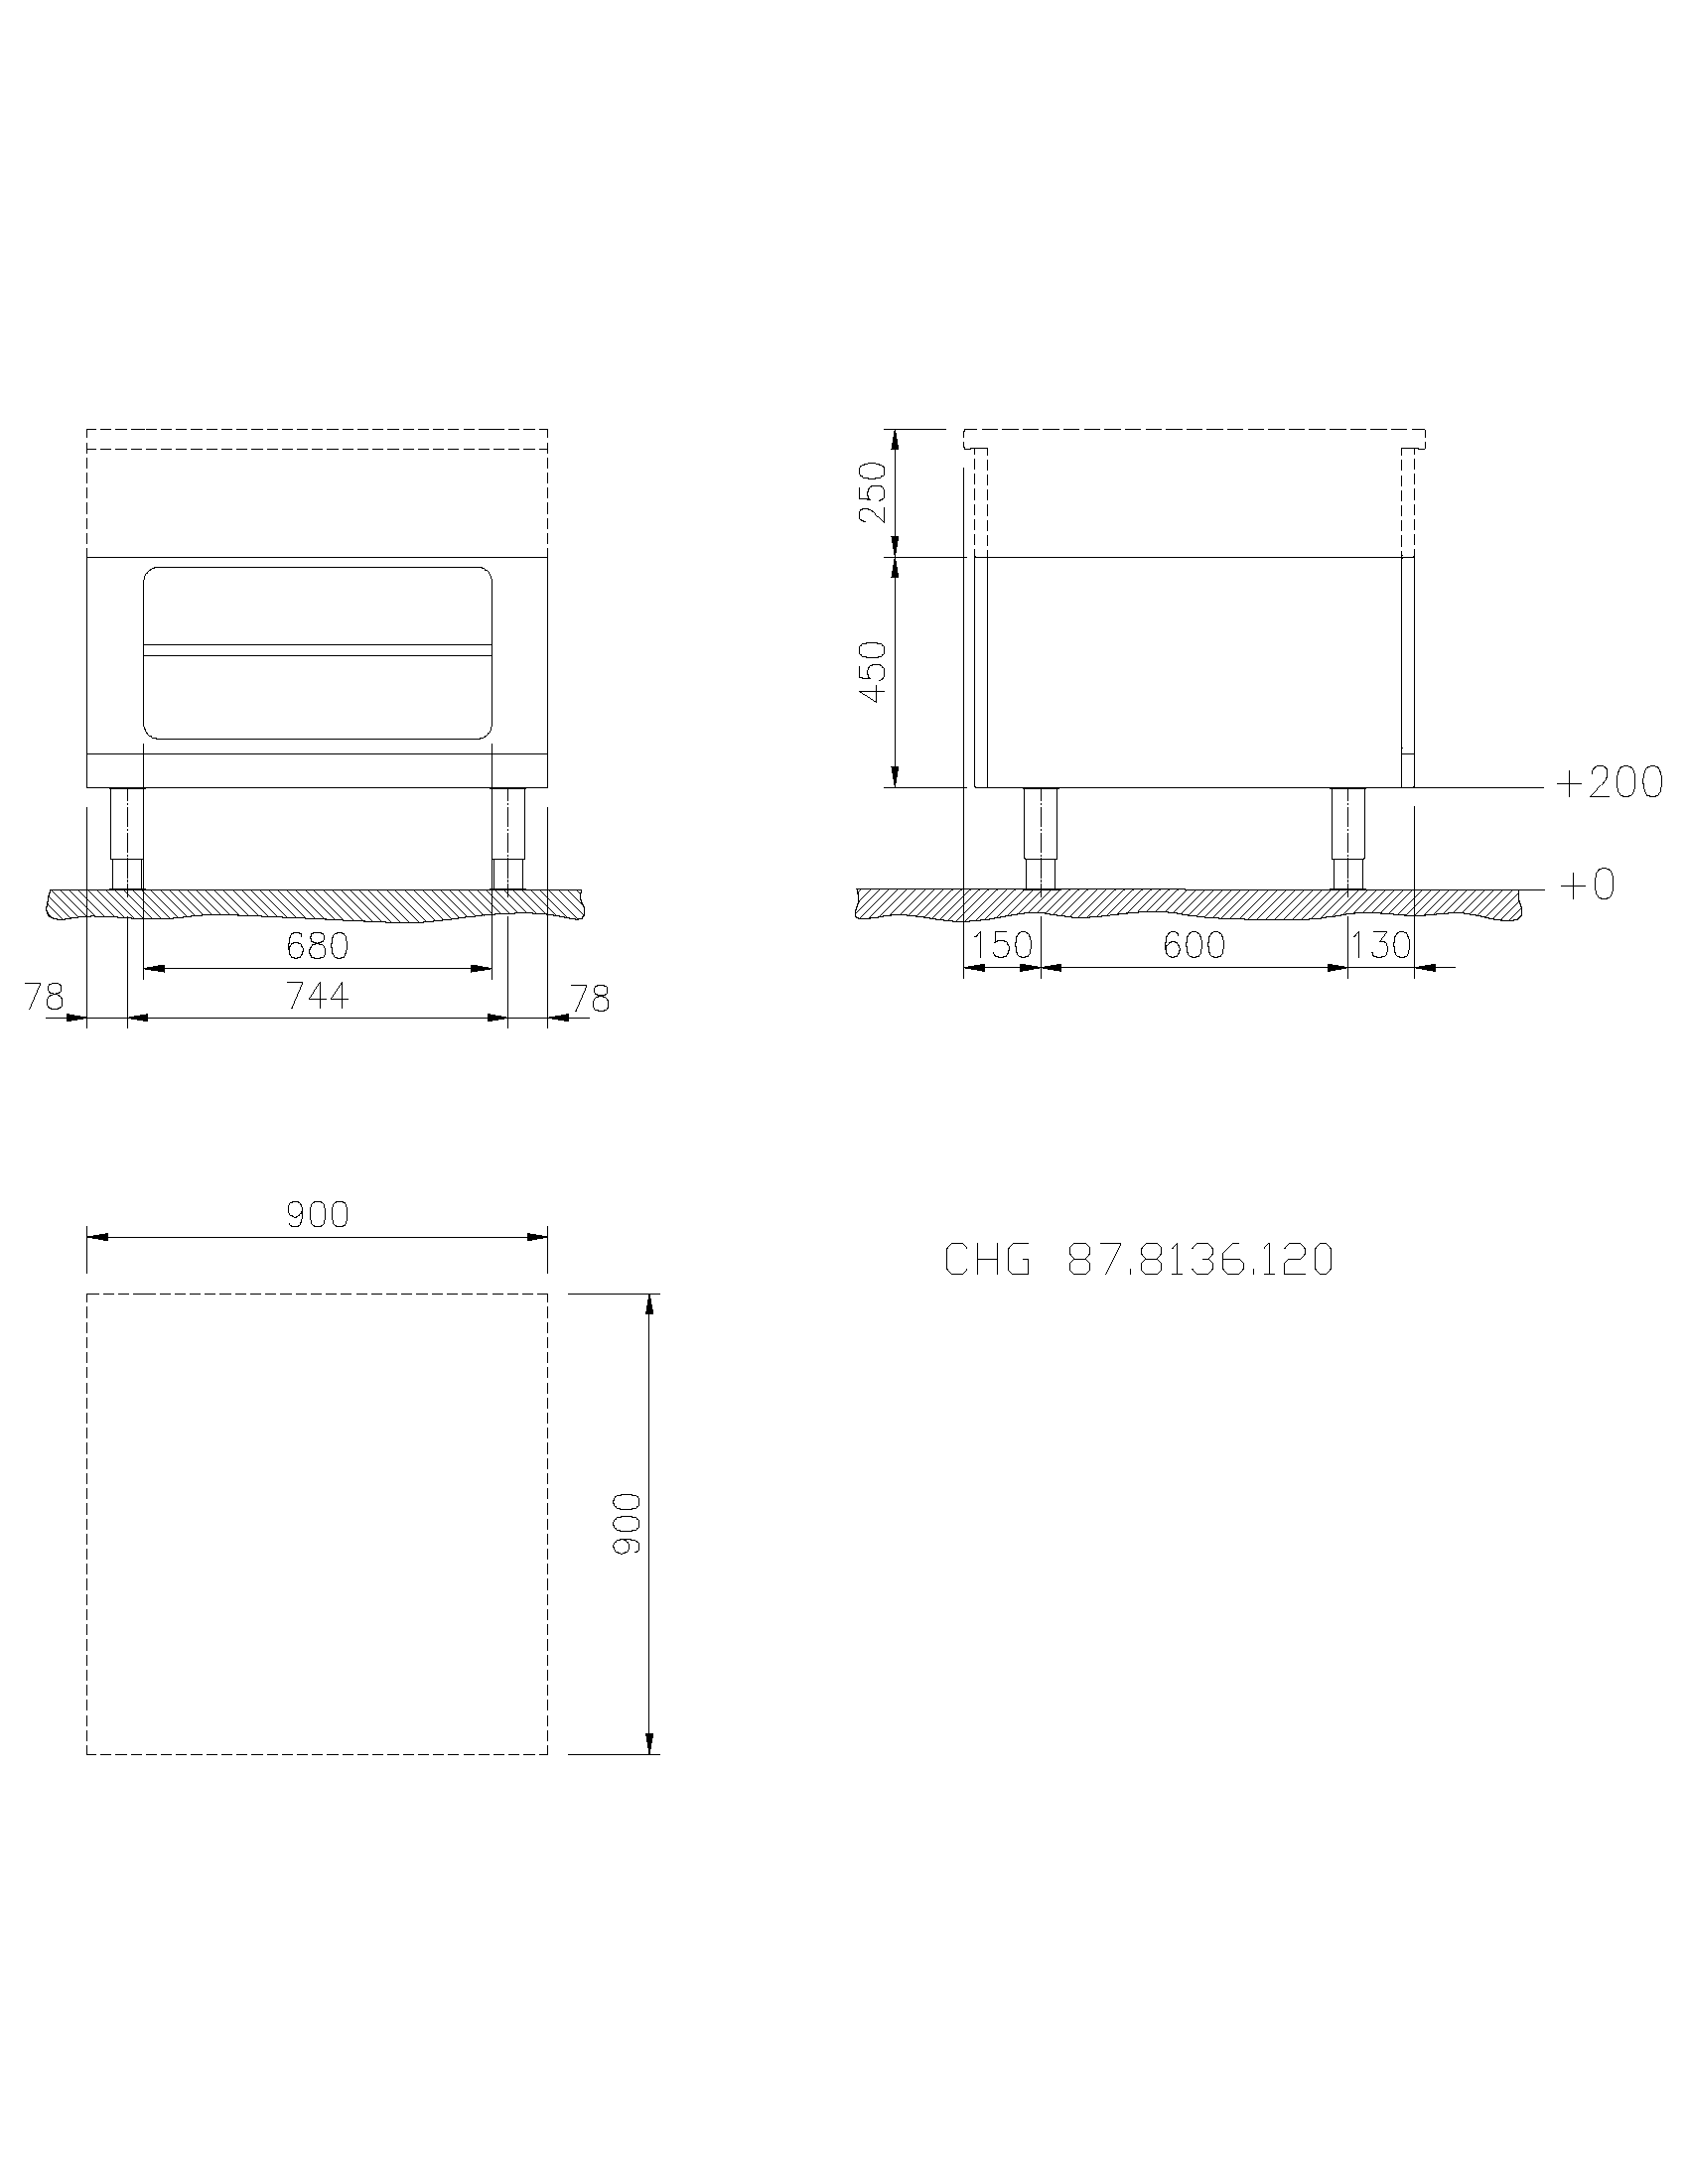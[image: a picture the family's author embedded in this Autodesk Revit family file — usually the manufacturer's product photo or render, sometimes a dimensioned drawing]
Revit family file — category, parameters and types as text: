
# Revit family: QF_ELECTROLUXPROFESSIONAL_589820_MCBAEAD1DM
name_source: partatom
category: Attrezzature speciali
units: mm (PartAtom-declared; Revit-internal decimal feet)

## family parameters
Basato su piano di lavoro = No
Condiviso = No
Punto di calcolo locali = No
Quota connettore circolare = Usa diametro
Sempre verticale = Sì
Taglio con vuoti quando caricato = No
Tipo di parte = Normale

## types (1)
- Standard
    Accessory = Sì
    Cold Water Size = 1"
    Compressed Air Pressure = 0.00 psi
    Compressed Air Size = 0"
    Compressed Air Volume = 0 GPM
    Condensate Return Size = 0"
    Cycle = 50 Hz
    Depth Actual = 900 mm  [stored 2.95276 ft]
    Descrizione = BAINM,1/1GN,TAP(B)1S,400X900X700 MARINE
    Direct Waste Size = 1"
    Gas Input Pressure = 0.0
    Gas KW = 0
    Gas Size = 0"
    HP = 2 HP
    Height Actual = 700 mm  [stored 2.29659 ft]
    Hot Water Size = 1"
    Item Number = 589820
    Length Actual = 400 mm  [stored 1.31234 ft]
    Modello = MCBAEAD1DM
    Phase = 3
    Produttore = Electrolux Professional
    Prospetto di default = 0 mm  [stored 0 ft]
    Refrigerant Compressor Remote = Sì
    Refrigeration Liquid Line Size = 0 mm  [stored 0 ft]
    Refrigeration Suction Line Size = 0 mm  [stored 0 ft]
    Steam Consumption per Hour = 0
    Steam Supply Maximum Pressure = 0.00 psi
    Steam Supply Minimum Pressure = 0.00 psi
    Steam Supply Size = 0"
    URL = https://www.electroluxprofessional.com
    URL Manufacturer = https://www.electroluxprofessional.com
    Volts = 440 V
    Watts = 1500 W
    Weight = 43.00 kg

note: source unit labels omitted for Gas Input Pressure — the stored unit's dimension contradicts the parameter name (converter mislabeling)

note: [stored X ft] marks values corroborated as IEEE doubles in the binary element streams (Revit-internal decimal feet)

## geometry (parser evidence)
native form markers: Blend x1, Sweep x12
no freeform markers — native parametric forms only
